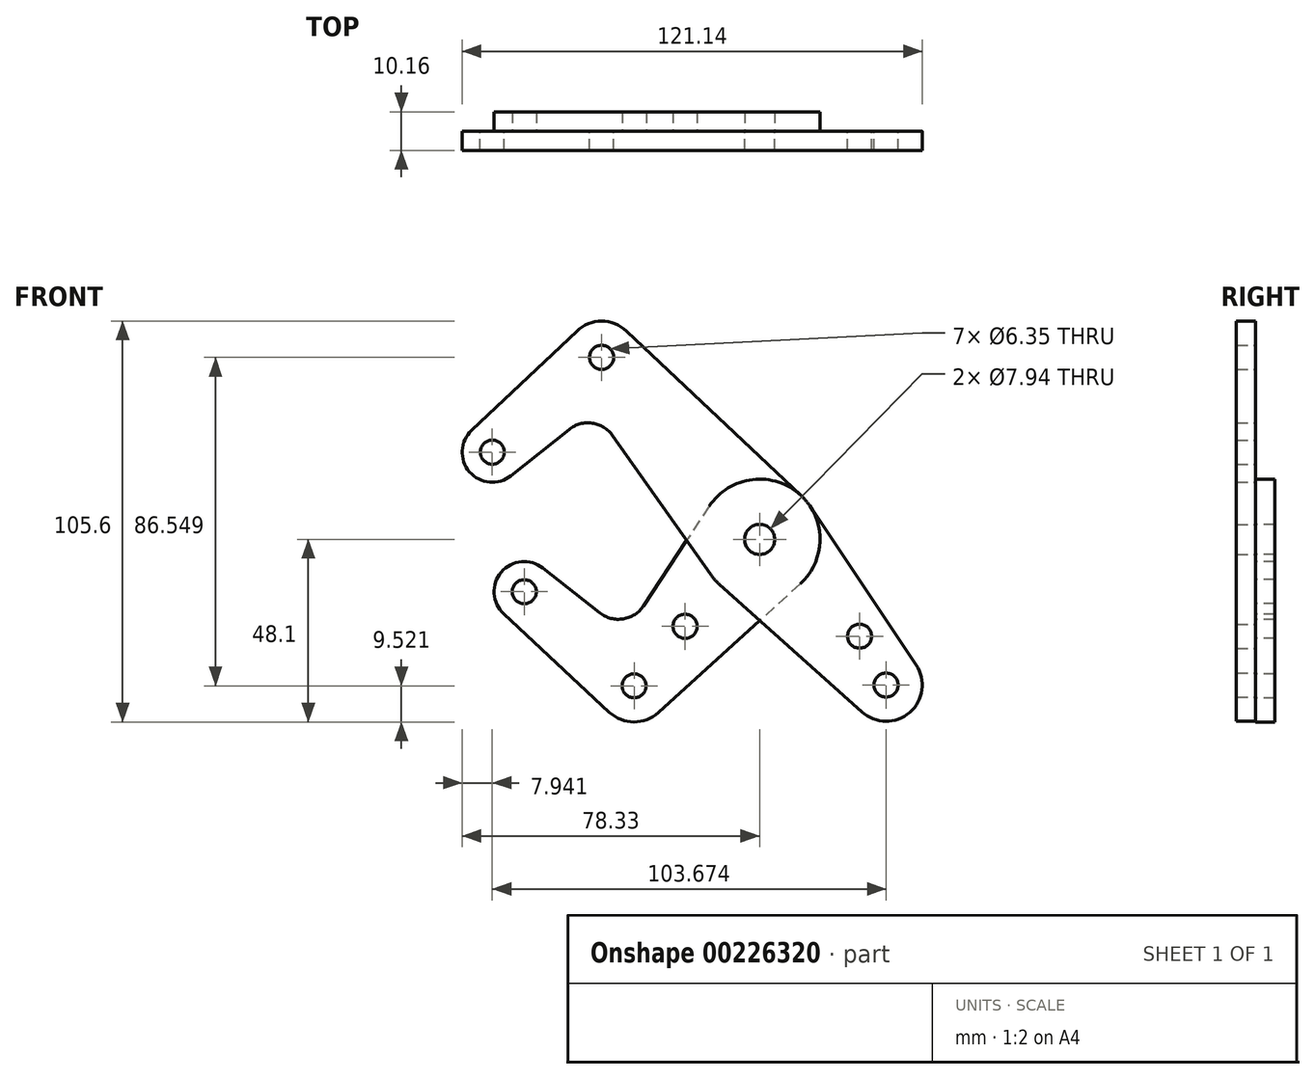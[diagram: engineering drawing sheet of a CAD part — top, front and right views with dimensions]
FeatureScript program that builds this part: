
annotation { "Feature Type Name" : "Feature", "Feature Type Description" : "" }
export const myFeature = defineFeature(function(context is Context, id is Id, definition is map)
    precondition{}
    {
        {
            var Q0;
            Q0=qCreatedBy(makeId("Front.planeOp"),FACE);
            var sketch = newSketch(context, id + "F0", { "sketchPlane" : qUnion([Q0])});
            skLineSegment(sketch, "E0", {"start": v(-41.6, 47.97) * mm, "end": v(41.6, -47.97) * mm, "construction": true});
            skCircle(sketch, "E1", {"center": v(0, 0) * mm, "radius": 3.18 * mm});
            skCircle(sketch, "E2", {"center": v(33.29, -38.38) * mm, "radius": 3.18 * mm});
            skCircle(sketch, "E3", {"center": v(-41.6, 47.97) * mm, "radius": 3.18 * mm});
            skCircle(sketch, "E4", {"center": v(-70.39, 23) * mm, "radius": 3.18 * mm});
            skLineSegment(sketch, "E5", {"start": v(-41.6, 47.97) * mm, "end": v(-70.39, 23) * mm, "construction": true});
            skCircle(sketch, "E6", {"center": v(33.29, -38.38) * mm, "radius": 9.53 * mm});
            skCircle(sketch, "E7", {"center": v(-70.39, 23) * mm, "radius": 7.94 * mm});
            skCircle(sketch, "E8", {"center": v(-41.6, 47.97) * mm, "radius": 9.53 * mm});
            skLineSegment(sketch, "E9", {"start": v(-75.83, 28.78) * mm, "end": v(-48.14, 54.9) * mm});
            skLineSegment(sketch, "E10", {"start": v(-65.44, 16.8) * mm, "end": v(-50.15, 28.98) * mm});
            skCircle(sketch, "E11", {"center": v(0, 0) * mm, "radius": 15.88 * mm});
            skLineSegment(sketch, "E12", {"start": v(-35.07, 54.9) * mm, "end": v(10.9, 11.55) * mm});
            skLineSegment(sketch, "E13", {"start": v(-38.72, 27.35) * mm, "end": v(-12.97, -9.15) * mm});
            skLineSegment(sketch, "E14", {"start": v(-10.6, -11.82) * mm, "end": v(26.93, -45.47) * mm});
            skLineSegment(sketch, "E15", {"start": v(13.2, 8.82) * mm, "end": v(41.2, -33.08) * mm});
            skArc(sketch, "E16.filletArc", {"start": v(-38.72, 27.35) * mm, "mid": v(-44.08, 30.63) * mm, "end": v(-50.15, 28.98) * mm});
            skLineSegment(sketch, "E17", {"start": v(0, 0) * mm, "end": v(-33.05, -38.58) * mm, "construction": true});
            skLineSegment(sketch, "E18", {"start": v(-33.05, -38.58) * mm, "end": v(-61.98, -13.8) * mm, "construction": true});
            skCircle(sketch, "E19", {"center": v(-61.98, -13.8) * mm, "radius": 3.18 * mm});
            skCircle(sketch, "E20", {"center": v(-33.05, -38.58) * mm, "radius": 3.18 * mm});
            skCircle(sketch, "E21", {"center": v(-61.98, -13.8) * mm, "radius": 7.94 * mm});
            skCircle(sketch, "E22", {"center": v(-33.05, -38.58) * mm, "radius": 9.53 * mm});
            skLineSegment(sketch, "E23", {"start": v(-57.08, -7.55) * mm, "end": v(-42.08, -19.35) * mm});
            skLineSegment(sketch, "E24", {"start": v(-67.4, -19.6) * mm, "end": v(-39.54, -45.55) * mm});
            skLineSegment(sketch, "E25", {"start": v(-13.25, 8.74) * mm, "end": v(-30.55, -17.48) * mm});
            skLineSegment(sketch, "E26", {"start": v(10.67, -11.75) * mm, "end": v(-26.65, -45.63) * mm});
            skArc(sketch, "E27.filletArc", {"start": v(-42.08, -19.35) * mm, "mid": v(-35.9, -20.95) * mm, "end": v(-30.55, -17.48) * mm});
            skCircle(sketch, "E28", {"center": v(-19.62, -22.9) * mm, "radius": 3.18 * mm});
            skCircle(sketch, "E29", {"center": v(26.32, -25.5) * mm, "radius": 3.18 * mm});
            skLineSegment(sketch, "E30", {"start": v(26.32, -25.5) * mm, "end": v(23.92, -27.58) * mm, "construction": true});
            skCircle(sketch, "E31", {"center": v(0, 0) * mm, "radius": 3.97 * mm});
            skSolve(sketch);
        }
        {
            var Q0;
            {var subQ1=sQuery(id+"F0.wireOp",EDGE,"E9");Q0=makeQuery(id+"F0.imprint","IMPRINT",FACE,{"disambiguationData":[TD([[makeQuery(id+"F0.imprint","IMPRINT",EDGE,{"derivedFrom":subQ1}),-1.0]])]});}
            var Q1;
            Q1=makeQuery(id+"F0.imprint","IMPRINT",FACE,{"disambiguationData":[TD([[makeQuery(id+"F0.imprint","IMPRINT",EDGE,{"derivedFrom":sQuery(id+"F0.wireOp",EDGE,"E4")}),-1.0]])]});
            var Q2;
            Q2=makeQuery(id+"F0.imprint","IMPRINT",FACE,{"disambiguationData":[TD([[makeQuery(id+"F0.imprint","IMPRINT",EDGE,{"derivedFrom":sQuery(id+"F0.wireOp",EDGE,"E3")}),-1.0]])]});
            var Q3;
            Q3=makeQuery(id+"F0.imprint","IMPRINT",FACE,{"disambiguationData":[TD([[makeQuery(id+"F0.imprint","IMPRINT",EDGE,{"derivedFrom":sQuery(id+"F0.wireOp",EDGE,"E31")}),-1.0]])]});
            var Q4;
            {var subQ0=sQuery(id+"F0.wireOp",EDGE,"E15");Q4=makeQuery(id+"F0.imprint","IMPRINT",FACE,{"disambiguationData":[TD([[makeQuery(id+"F0.imprint","IMPRINT",EDGE,{"derivedFrom":subQ0}),-1.0]])]});}
            var Q5;
            Q5=makeQuery(id+"F0.imprint","IMPRINT",FACE,{"disambiguationData":[TD([[makeQuery(id+"F0.imprint","IMPRINT",EDGE,{"derivedFrom":sQuery(id+"F0.wireOp",EDGE,"E2")}),-1.0]])]});
            var Q6;
            {var subQ0=sQuery(id+"F0.wireOp",EDGE,"E14");var subQ1=sQuery(id+"F0.wireOp",EDGE,"E11");var subQ2=makeQuery(id+"F0.imprint","INTERSECT",VERTEX,{"derivedFrom":[subQ1,subQ0]});Q6=makeQuery(id+"F0.imprint","IMPRINT",FACE,{"disambiguationData":[TD([[makeQuery(id+"F0.imprint","IMPRINT",EDGE,{"disambiguationData":[TD([[subQ2,-1.0]])],"derivedFrom":subQ1}),-1.0]])]});}
            var Q7;
            {var subQ0=sQuery(id+"F0.wireOp",EDGE,"E13");var subQ1=sQuery(id+"F0.wireOp",EDGE,"E11");var subQ2=makeQuery(id+"F0.imprint","INTERSECT",VERTEX,{"derivedFrom":[subQ1,subQ0]});Q7=makeQuery(id+"F0.imprint","IMPRINT",FACE,{"disambiguationData":[TD([[makeQuery(id+"F0.imprint","IMPRINT",EDGE,{"disambiguationData":[TD([[subQ2,1.0]])],"derivedFrom":subQ1}),-1.0]])]});}
            extrude(context, id + "F1", {"entities" : qUnion([Q0, Q1, Q2, Q3, Q4, Q5, Q6, Q7]), "depth" : 5.08 * mm});
        }
        {
            var Q0;
            Q0=makeQuery(id+"F0.imprint","IMPRINT",FACE,{"disambiguationData":[TD([[makeQuery(id+"F0.imprint","IMPRINT",EDGE,{"derivedFrom":sQuery(id+"F0.wireOp",EDGE,"E31")}),-1.0]])]});
            var Q1;
            {var subQ0=sQuery(id+"F0.wireOp",EDGE,"E14");var subQ1=sQuery(id+"F0.wireOp",EDGE,"E11");var subQ2=makeQuery(id+"F0.imprint","INTERSECT",VERTEX,{"derivedFrom":[subQ1,subQ0]});Q1=makeQuery(id+"F0.imprint","IMPRINT",FACE,{"disambiguationData":[TD([[makeQuery(id+"F0.imprint","IMPRINT",EDGE,{"disambiguationData":[TD([[subQ2,-1.0]])],"derivedFrom":subQ1}),-1.0]])]});}
            var Q2;
            {var subQ0=sQuery(id+"F0.wireOp",EDGE,"E13");var subQ1=sQuery(id+"F0.wireOp",EDGE,"E11");var subQ2=makeQuery(id+"F0.imprint","INTERSECT",VERTEX,{"derivedFrom":[subQ1,subQ0]});Q2=makeQuery(id+"F0.imprint","IMPRINT",FACE,{"disambiguationData":[TD([[makeQuery(id+"F0.imprint","IMPRINT",EDGE,{"disambiguationData":[TD([[subQ2,1.0]])],"derivedFrom":subQ1}),-1.0]])]});}
            var Q3;
            {var subQ10=sQuery(id+"F0.wireOp",EDGE,"E23");Q3=makeQuery(id+"F0.imprint","IMPRINT",FACE,{"disambiguationData":[TD([[makeQuery(id+"F0.imprint","IMPRINT",EDGE,{"derivedFrom":subQ10}),-1.0]])]});}
            var Q4;
            Q4=makeQuery(id+"F0.imprint","IMPRINT",FACE,{"disambiguationData":[TD([[makeQuery(id+"F0.imprint","IMPRINT",EDGE,{"derivedFrom":sQuery(id+"F0.wireOp",EDGE,"E20")}),-1.0]])]});
            var Q5;
            Q5=makeQuery(id+"F0.imprint","IMPRINT",FACE,{"disambiguationData":[TD([[makeQuery(id+"F0.imprint","IMPRINT",EDGE,{"derivedFrom":sQuery(id+"F0.wireOp",EDGE,"E19")}),-1.0]])]});
            extrude(context, id + "F2", {"entities" : qUnion([Q0, Q1, Q2, Q3, Q4, Q5]), "oppositeDirection" : true, "depth" : 5.08 * mm});
        }
    });
